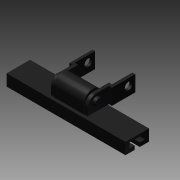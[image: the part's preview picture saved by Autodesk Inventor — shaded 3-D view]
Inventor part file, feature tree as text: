
AUTODESK INVENTOR PART (.ipt)
format: ipt  version: 2012 (Build 160160000, 160)  size: 147,456 bytes
history: native  units: in
note: dims shown in document units (in); Inventor stores cm internally (conversion verified against a paired STEP export)
features: extrude x4, sketch x4, other x1, imported_body x1
ambient origin geometry x8: Origin, YZ Plane, XZ Plane, XY Plane, X Axis, Y Axis, Z Axis, Center Point
feature tree (10):
  other  "TANKTREAD_4092"
  imported_body  "Base1"
  extrude  "Extrusion1"  Depth=0.0984in
  extrude  "Extrusion2"  Depth=0.0394in TaperAngle=0.0deg
  extrude  "Extrusion3"  [1 undecoded]
  extrude  "Extrusion4"  [1 undecoded]
  sketch  "Sketch1"  dims[d0=0.3937in d1=0.0in d2=0.0984in]
  sketch  "Sketch2"  dims[d3=0.0394in d4=0.0in d5=0.0394in d6=0.0in]
  sketch  "Sketch3"  dims[d7=0.0394in d8=0.0in]
  sketch  "Sketch4"
note: 2 required parameter values undecoded (feature->parameter linkage not recoverable at this tier; creation-order binding heuristic only, values carry confidence <= 0.55)
